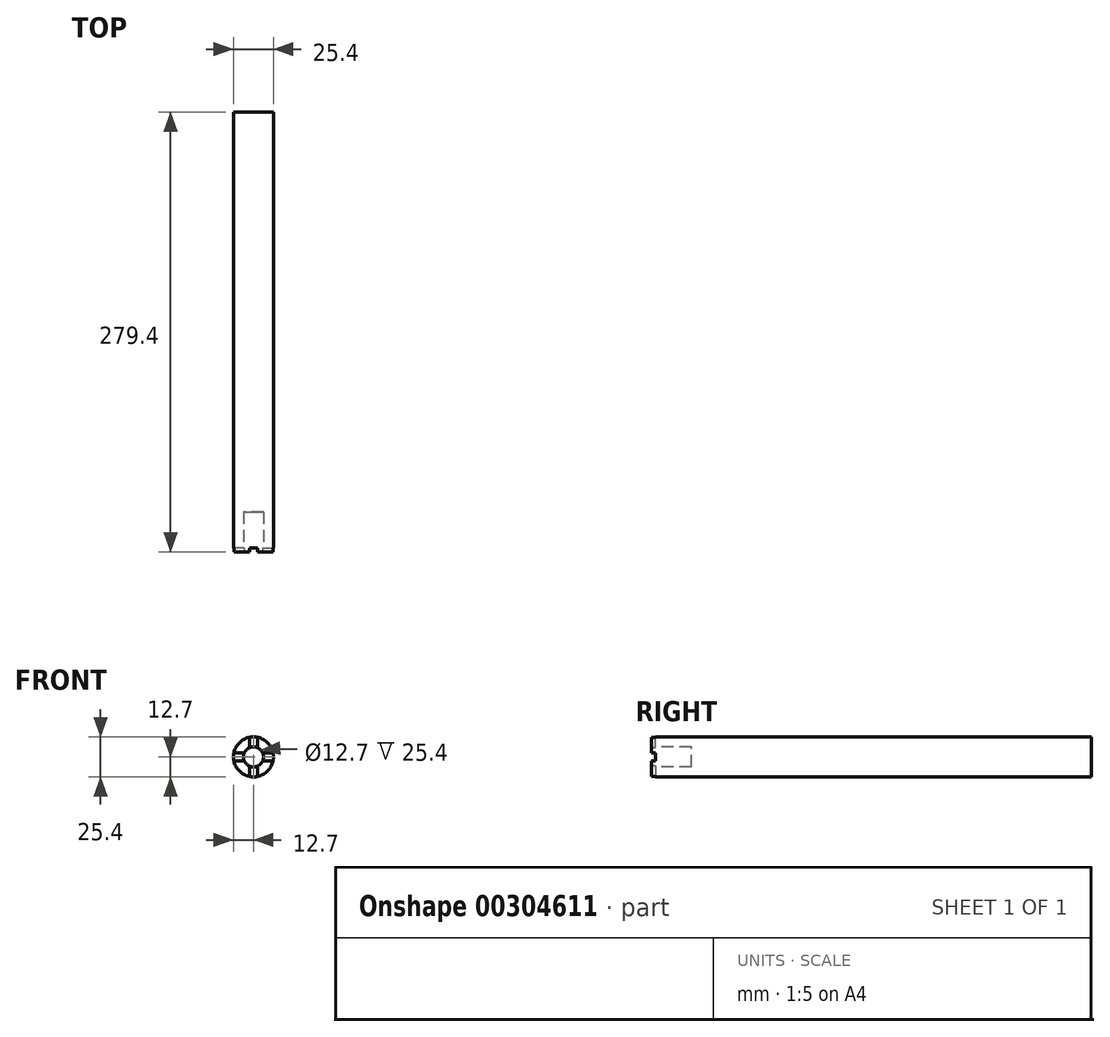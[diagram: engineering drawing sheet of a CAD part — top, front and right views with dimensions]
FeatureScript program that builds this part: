
annotation { "Feature Type Name" : "Feature", "Feature Type Description" : "" }
export const myFeature = defineFeature(function(context is Context, id is Id, definition is map)
    precondition{}
    {
        {
            var Q0;
            Q0=qCreatedBy(makeId("Front.planeOp"),FACE);
            var sketch = newSketch(context, id + "F0", { "sketchPlane" : qUnion([Q0])});
            skCircle(sketch, "E0", {"center": v(0, 0) * mm, "radius": 12.7 * mm});
            skSolve(sketch);
        }
        {
            var Q0;
            Q0 = qSketchRegion(id + "F0", true);
            extrude(context, id + "F1", {"entities" : qUnion([Q0]), "depth" : 279.4 * mm});
        }
        {
            var Q0;
            Q0=makeQuery(id+"F1.opExtrude","CAP_FACE",FACE,{"disambiguationData":[OSD([sQuery(id+"F0.wireOp",EDGE,"E0")])],"isStart":false});
            var sketch = newSketch(context, id + "F2", { "sketchPlane" : qUnion([Q0])});
            skCircle(sketch, "E1", {"center": v(0, 0) * mm, "radius": 6.35 * mm});
            skSolve(sketch);
        }
        {
            var Q0;
            Q0=makeQuery(id+"F2.imprint","IMPRINT",FACE,{"disambiguationData":[TD([[makeQuery(id+"F2.imprint","IMPRINT",EDGE,{"derivedFrom":sQuery(id+"F2.wireOp",EDGE,"E1")}),1.0]])]});
            extrude(context, id + "F3", {"entities" : qUnion([Q0]), "operationType" : NewBodyOperationType.REMOVE, "oppositeDirection" : true, "depth" : 25.4 * mm});
        }
        {
            var Q0;
            Q0=makeQuery(id+"F1.opExtrude","CAP_FACE",FACE,{"disambiguationData":[OSD([sQuery(id+"F0.wireOp",EDGE,"E0")])],"isStart":false});
            var sketch = newSketch(context, id + "F4", { "sketchPlane" : qUnion([Q0])});
            skLineSegment(sketch, "E2", {"start": v(2.54, 12.44) * mm, "end": v(-2.54, 12.44) * mm, "construction": true});
            skLineSegment(sketch, "E3", {"start": v(-2.54, 12.44) * mm, "end": v(-2.54, 5.82) * mm});
            skLineSegment(sketch, "E4", {"start": v(-2.54, -12.44) * mm, "end": v(2.54, -12.44) * mm, "construction": true});
            skLineSegment(sketch, "E5", {"start": v(2.54, 12.44) * mm, "end": v(2.54, 5.82) * mm});
            skLineSegment(sketch, "E6", {"start": v(12.44, 2.54) * mm, "end": v(5.82, 2.54) * mm});
            skLineSegment(sketch, "E7", {"start": v(-12.44, 2.54) * mm, "end": v(-12.44, -2.54) * mm, "construction": true});
            skLineSegment(sketch, "E8", {"start": v(-12.44, -2.54) * mm, "end": v(-5.82, -2.54) * mm});
            skLineSegment(sketch, "E9", {"start": v(12.44, -2.54) * mm, "end": v(12.44, 2.54) * mm, "construction": true});
            skLineSegment(sketch, "E10.trimOffspring", {"start": v(-5.82, 2.54) * mm, "end": v(-12.44, 2.54) * mm});
            skLineSegment(sketch, "E11.trimOffspring", {"start": v(5.82, -2.54) * mm, "end": v(12.44, -2.54) * mm});
            skLineSegment(sketch, "E12.trimOffspring", {"start": v(-2.54, -5.82) * mm, "end": v(-2.54, -12.44) * mm});
            skLineSegment(sketch, "E13.trimOffspring", {"start": v(2.54, -5.82) * mm, "end": v(2.54, -12.44) * mm});
            skLineSegment(sketch, "E14", {"start": v(-2.54, 12.44) * mm, "end": v(-2.54, 14.25) * mm});
            skLineSegment(sketch, "E15", {"start": v(-2.54, 14.25) * mm, "end": v(2.54, 14.25) * mm});
            skLineSegment(sketch, "E16", {"start": v(2.54, 14.25) * mm, "end": v(2.54, 12.44) * mm});
            skLineSegment(sketch, "E17", {"start": v(12.44, 2.54) * mm, "end": v(14.25, 2.54) * mm});
            skLineSegment(sketch, "E18", {"start": v(14.25, 2.54) * mm, "end": v(14.25, -2.54) * mm});
            skLineSegment(sketch, "E19", {"start": v(14.25, -2.54) * mm, "end": v(12.44, -2.54) * mm});
            skLineSegment(sketch, "E20", {"start": v(2.54, -12.44) * mm, "end": v(2.54, -14.25) * mm});
            skLineSegment(sketch, "E21", {"start": v(2.54, -14.25) * mm, "end": v(-2.54, -14.25) * mm});
            skLineSegment(sketch, "E22", {"start": v(-2.54, -14.25) * mm, "end": v(-2.54, -12.44) * mm});
            skLineSegment(sketch, "E23", {"start": v(-12.44, 2.54) * mm, "end": v(-14.25, 2.54) * mm});
            skLineSegment(sketch, "E24", {"start": v(-14.25, 2.54) * mm, "end": v(-14.25, -2.54) * mm});
            skLineSegment(sketch, "E25", {"start": v(-14.25, -2.54) * mm, "end": v(-12.44, -2.54) * mm});
            skCircle(sketch, "E26", {"center": v(0, 0) * mm, "radius": 6.35 * mm});
            skSolve(sketch);
        }
        {
            var Q0;
            Q0 = qSketchRegion(id + "F4", true);
            extrude(context, id + "F5", {"entities" : qUnion([Q0]), "operationType" : NewBodyOperationType.REMOVE, "oppositeDirection" : true, "depth" : 2.54 * mm});
        }
    });
